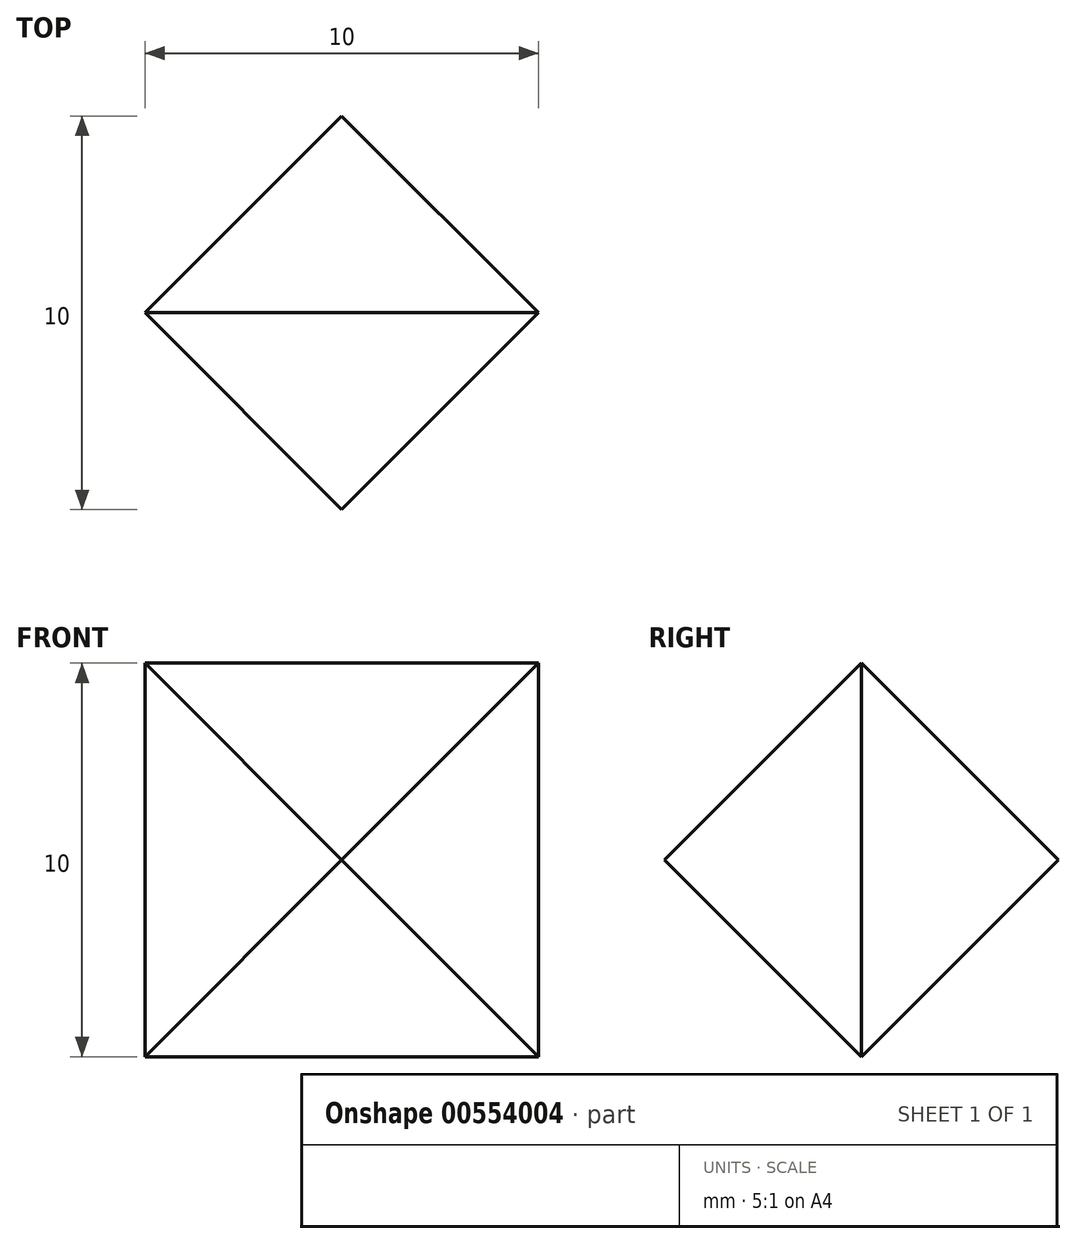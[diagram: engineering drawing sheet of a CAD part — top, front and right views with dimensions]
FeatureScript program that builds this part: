
annotation { "Feature Type Name" : "Feature", "Feature Type Description" : "" }
export const myFeature = defineFeature(function(context is Context, id is Id, definition is map)
    precondition{}
    {
        {
            var Q0;
            Q0=qCreatedBy(makeId("Front.planeOp"),FACE);
            var sketch = newSketch(context, id + "F0", { "sketchPlane" : qUnion([Q0])});
            skLineSegment(sketch, "E0.bottom", {"start": v(-5, 5) * mm, "end": v(5, 5) * mm});
            skLineSegment(sketch, "E0.top", {"start": v(-5, -5) * mm, "end": v(5, -5) * mm});
            skLineSegment(sketch, "E0.left", {"start": v(-5, 5) * mm, "end": v(-5, -5) * mm});
            skLineSegment(sketch, "E0.right", {"start": v(5, 5) * mm, "end": v(5, -5) * mm});
            skPoint(sketch, "E1", {"position": v(0, 0) * mm});
            skPoint(sketch, "E1.positionSnap0", {"position": v(0, 5) * mm});
            skPoint(sketch, "E1.positionSnap1", {"position": v(5, 0) * mm});
            skSolve(sketch);
        }
        {
            var Q0;
            Q0=makeQuery(id+"F0.imprint","IMPRINT",FACE,{"disambiguationData":[TD([[makeQuery(id+"F0.imprint","IMPRINT",EDGE,{"derivedFrom":sQuery(id+"F0.wireOp",EDGE,"5Z7USOKa-lhl3-uVCC-a3Aj-KD8gw8EUCcGV")}),1.0]])]});
            var Q1;
            Q1=makeQuery(id+"F0.imprint","IMPRINT",FACE,{"disambiguationData":[TD([[makeQuery(id+"F0.imprint","IMPRINT",EDGE,{"derivedFrom":sQuery(id+"F0.wireOp",EDGE,"E0.bottom")}),-1.0]])]});
            extrude(context, id + "F1", {"entities" : qUnion([Q0, Q1]), "endBound" : BoundingType.SYMMETRIC, "depth" : 10 * mm, "offsetDistance" : 25 * mm});
        }
        {
            var Q0;
            Q0=makeQuery(id+"F1.opExtrude","CAP_FACE",FACE,{"disambiguationData":[OSD([sQuery(id+"F0.wireOp",EDGE,"E0.bottom"),sQuery(id+"F0.wireOp",EDGE,"E0.top"),sQuery(id+"F0.wireOp",EDGE,"E0.left"),sQuery(id+"F0.wireOp",EDGE,"E0.right")])],"isStart":false});
            var Q1;
            Q1=makeQuery(id+"F1.opExtrude","CAP_FACE",FACE,{"disambiguationData":[OSD([sQuery(id+"F0.wireOp",EDGE,"E0.bottom"),sQuery(id+"F0.wireOp",EDGE,"E0.top"),sQuery(id+"F0.wireOp",EDGE,"E0.left"),sQuery(id+"F0.wireOp",EDGE,"E0.right")])],"isStart":true});
            chamfer(context, id + "F2", {"entities" : qUnion([Q0, Q1]), "chamferType" : ChamferType.OFFSET_ANGLE, "width" : 5 * mm, "oppositeDirection" : false, "angle" : 45 * degree, "tangentPropagation" : true});
        }
    });
